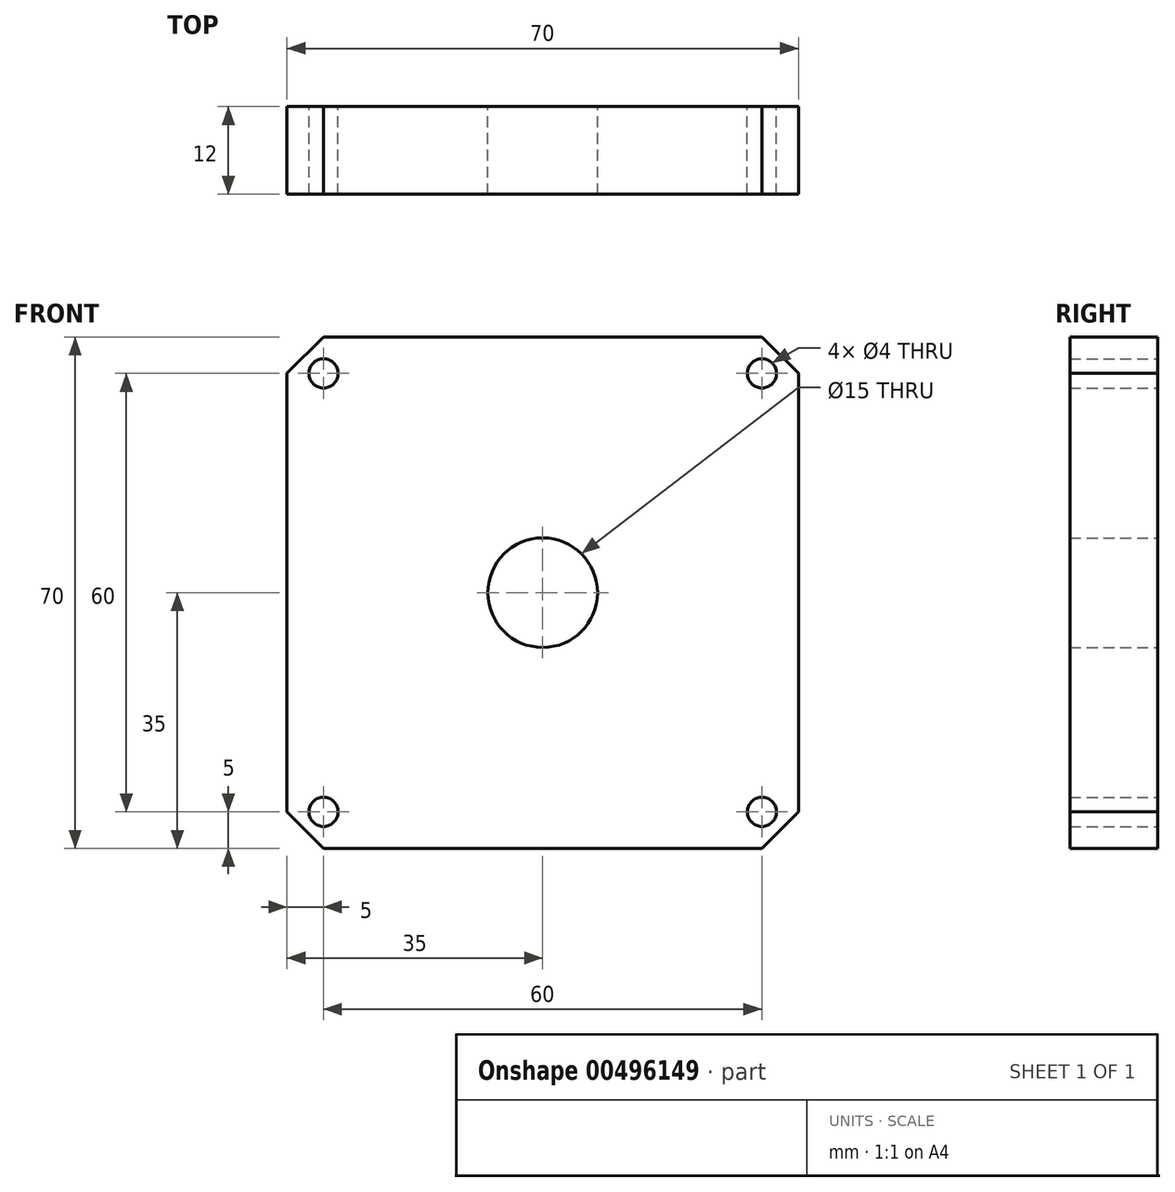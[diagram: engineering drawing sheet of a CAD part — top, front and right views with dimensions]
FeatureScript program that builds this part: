
annotation { "Feature Type Name" : "Feature", "Feature Type Description" : "" }
export const myFeature = defineFeature(function(context is Context, id is Id, definition is map)
    precondition{}
    {
        {
            var Q0;
            Q0=qCreatedBy(makeId("Front.planeOp"),FACE);
            var sketch = newSketch(context, id + "F0", { "sketchPlane" : qUnion([Q0])});
            skLineSegment(sketch, "E0.bottom", {"start": v(35, 35) * mm, "end": v(-35, 35) * mm});
            skLineSegment(sketch, "E0.top", {"start": v(35, -35) * mm, "end": v(-35, -35) * mm});
            skLineSegment(sketch, "E0.left", {"start": v(35, 35) * mm, "end": v(35, -35) * mm});
            skLineSegment(sketch, "E0.right", {"start": v(-35, 35) * mm, "end": v(-35, -35) * mm});
            skPoint(sketch, "E0.middle", {"position": v(0, 0) * mm});
            skCircle(sketch, "E1", {"center": v(0, 0) * mm, "radius": 7.5 * mm});
            skPoint(sketch, "E2", {"position": v(-30, 30) * mm});
            skPoint(sketch, "E3", {"position": v(30, 30) * mm});
            skPoint(sketch, "E4", {"position": v(30, -30) * mm});
            skPoint(sketch, "E5", {"position": v(-30, -30) * mm});
            skCircle(sketch, "E6", {"center": v(-30, 30) * mm, "radius": 2 * mm});
            skCircle(sketch, "E7", {"center": v(30, 30) * mm, "radius": 2 * mm});
            skCircle(sketch, "E8", {"center": v(30, -30) * mm, "radius": 2 * mm});
            skCircle(sketch, "E9", {"center": v(-30, -30) * mm, "radius": 2 * mm});
            skSolve(sketch);
        }
        {
            var Q0;
            Q0=qSketchRegion(id+"F0",true);
            extrude(context, id + "F1", {"entities" : qUnion([Q0]), "depth" : 12 * mm});
        }
        {
            var Q0;
            Q0=makeQuery(id+"F1.opExtrude","SWEPT_EDGE",EDGE,{"disambiguationData":[OSD([sQuery(id+"F0.wireOp",EDGE,"E0.bottom"),sQuery(id+"F0.wireOp",EDGE,"E0.right")])]});
            var Q1;
            Q1=makeQuery(id+"F1.opExtrude","SWEPT_EDGE",EDGE,{"disambiguationData":[OSD([sQuery(id+"F0.wireOp",EDGE,"E0.bottom"),sQuery(id+"F0.wireOp",EDGE,"E0.left")])]});
            var Q2;
            Q2=makeQuery(id+"F1.opExtrude","SWEPT_EDGE",EDGE,{"disambiguationData":[OSD([sQuery(id+"F0.wireOp",EDGE,"E0.top"),sQuery(id+"F0.wireOp",EDGE,"E0.left")])]});
            var Q3;
            Q3=makeQuery(id+"F1.opExtrude","SWEPT_EDGE",EDGE,{"disambiguationData":[OSD([sQuery(id+"F0.wireOp",EDGE,"E0.top"),sQuery(id+"F0.wireOp",EDGE,"E0.right")])]});
            chamfer(context, id + "F2", {"entities" : qUnion([Q0, Q1, Q2, Q3]), "width" : 5 * mm, "tangentPropagation" : true});
        }
    });
